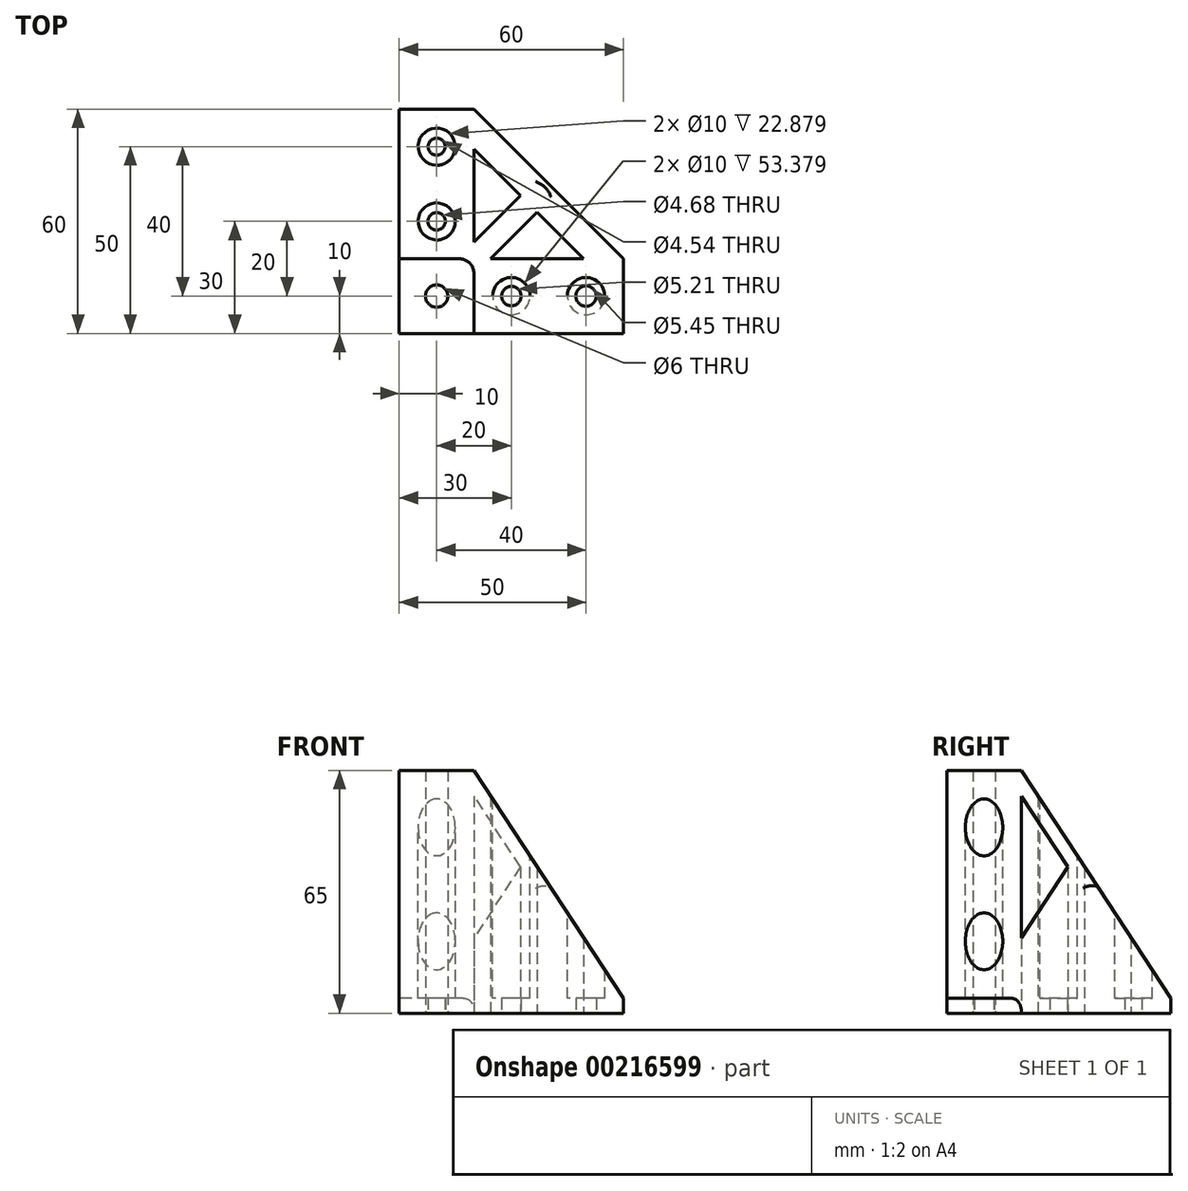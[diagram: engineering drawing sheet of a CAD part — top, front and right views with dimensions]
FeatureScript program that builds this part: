
annotation { "Feature Type Name" : "Feature", "Feature Type Description" : "" }
export const myFeature = defineFeature(function(context is Context, id is Id, definition is map)
    precondition{}
    {
        {
            var Q0;
            Q0=qCreatedBy(makeId("Top.planeOp"),FACE);
            var sketch = newSketch(context, id + "F0", { "sketchPlane" : qUnion([Q0])});
            skLineSegment(sketch, "E0", {"start": v(0, 0) * mm, "end": v(0, 60) * mm});
            skLineSegment(sketch, "E1", {"start": v(0, 60) * mm, "end": v(20, 60) * mm});
            skLineSegment(sketch, "E2", {"start": v(0, 0) * mm, "end": v(60, 0) * mm});
            skLineSegment(sketch, "E3", {"start": v(60, 0) * mm, "end": v(60, 20) * mm});
            skLineSegment(sketch, "E4", {"start": v(20, 60) * mm, "end": v(60, 20) * mm});
            skLineSegment(sketch, "E5", {"start": v(20, 49.4) * mm, "end": v(49.4, 20) * mm, "construction": true});
            skLineSegment(sketch, "E6", {"start": v(49.4, 20) * mm, "end": v(20, 20) * mm, "construction": true});
            skLineSegment(sketch, "E7", {"start": v(20, 20) * mm, "end": v(20, 49.4) * mm, "construction": true});
            skLineSegment(sketch, "E8", {"start": v(24.48, 20) * mm, "end": v(36.94, 32.46) * mm});
            skLineSegment(sketch, "E9", {"start": v(20, 20) * mm, "end": v(34.7, 34.7) * mm, "construction": true});
            skLineSegment(sketch, "E10.MirrorCS", {"start": v(20, 24.48) * mm, "end": v(32.46, 36.94) * mm});
            skLineSegment(sketch, "E11", {"start": v(20, 49.4) * mm, "end": v(20, 24.48) * mm});
            skLineSegment(sketch, "E12", {"start": v(20, 49.4) * mm, "end": v(32.46, 36.94) * mm});
            skLineSegment(sketch, "E13", {"start": v(24.48, 20) * mm, "end": v(49.4, 20) * mm});
            skLineSegment(sketch, "E14", {"start": v(36.94, 32.46) * mm, "end": v(49.4, 20) * mm});
            skSolve(sketch);
        }
        {
            var Q0;
            Q0 = qSketchRegion(id + "F0", true);
            extrude(context, id + "F1", {"entities" : qUnion([Q0]), "depth" : 65 * mm});
        }
        {
            var Q0;
            Q0=makeQuery(id+"F1.opExtrude","SWEPT_FACE",FACE,{"disambiguationData":[OSD([sQuery(id+"F0.wireOp",EDGE,"E2")])]});
            var sketch = newSketch(context, id + "F2", { "sketchPlane" : qUnion([Q0])});
            skLineSegment(sketch, "E15", {"start": v(20, 65) * mm, "end": v(60, 4) * mm});
            skLineSegment(sketch, "E16", {"start": v(60, 4) * mm, "end": v(60, 65) * mm});
            skLineSegment(sketch, "E17", {"start": v(60, 65) * mm, "end": v(20, 65) * mm});
            skSolve(sketch);
        }
        {
            var Q0;
            Q0 = qSketchRegion(id + "F2", true);
            extrude(context, id + "F3", {"entities" : qUnion([Q0]), "operationType" : NewBodyOperationType.REMOVE, "endBound" : BoundingType.THROUGH_ALL, "oppositeDirection" : true, "depth" : 25 * mm});
        }
        {
            var Q0;
            Q0=makeQuery(id+"F1.opExtrude","SWEPT_FACE",FACE,{"disambiguationData":[OSD([sQuery(id+"F0.wireOp",EDGE,"E0")])]});
            var sketch = newSketch(context, id + "F4", { "sketchPlane" : qUnion([Q0])});
            skLineSegment(sketch, "E18", {"start": v(-60, 4) * mm, "end": v(-20, 65) * mm});
            skLineSegment(sketch, "E19", {"start": v(-20, 65) * mm, "end": v(-60, 65) * mm});
            skLineSegment(sketch, "E20", {"start": v(-60, 65) * mm, "end": v(-60, 4) * mm});
            skSolve(sketch);
        }
        {
            var Q0;
            Q0 = qSketchRegion(id + "F4", true);
            extrude(context, id + "F5", {"entities" : qUnion([Q0]), "operationType" : NewBodyOperationType.REMOVE, "endBound" : BoundingType.THROUGH_ALL, "oppositeDirection" : true, "depth" : 25 * mm});
        }
        {
            var Q0;
            Q0=makeQuery(id+"F1.opExtrude","CAP_FACE",FACE,{"disambiguationData":[OSD([sQuery(id+"F0.wireOp",EDGE,"E0"),sQuery(id+"F0.wireOp",EDGE,"E1"),sQuery(id+"F0.wireOp",EDGE,"E2"),sQuery(id+"F0.wireOp",EDGE,"E3"),sQuery(id+"F0.wireOp",EDGE,"E4"),sQuery(id+"F0.wireOp",EDGE,"E8"),sQuery(id+"F0.wireOp",EDGE,"E10.MirrorCS"),sQuery(id+"F0.wireOp",EDGE,"E11"),sQuery(id+"F0.wireOp",EDGE,"E12"),sQuery(id+"F0.wireOp",EDGE,"E13"),sQuery(id+"F0.wireOp",EDGE,"E14")])],"isStart":true});
            var sketch = newSketch(context, id + "F6", { "sketchPlane" : qUnion([Q0])});
            skCircle(sketch, "E21", {"center": v(10, -10) * mm, "radius": 2.5 * mm});
            skCircle(sketch, "E22", {"center": v(30, -10) * mm, "radius": 2.6 * mm});
            skCircle(sketch, "E23", {"center": v(50, -10) * mm, "radius": 2.73 * mm});
            skCircle(sketch, "E24", {"center": v(10, -30) * mm, "radius": 2.34 * mm});
            skCircle(sketch, "E25", {"center": v(10, -50) * mm, "radius": 2.27 * mm});
            skSolve(sketch);
        }
        {
            var Q0;
            Q0 = qSketchRegion(id + "F6", true);
            extrude(context, id + "F7", {"entities" : qUnion([Q0]), "operationType" : NewBodyOperationType.REMOVE, "endBound" : BoundingType.THROUGH_ALL, "oppositeDirection" : true, "depth" : 25 * mm});
        }
        {
            var Q0;
            Q0=makeQuery(id+"F1.opExtrude","CAP_FACE",FACE,{"disambiguationData":[OSD([sQuery(id+"F0.wireOp",EDGE,"E0"),sQuery(id+"F0.wireOp",EDGE,"E1"),sQuery(id+"F0.wireOp",EDGE,"E2"),sQuery(id+"F0.wireOp",EDGE,"E3"),sQuery(id+"F0.wireOp",EDGE,"E4"),sQuery(id+"F0.wireOp",EDGE,"E8"),sQuery(id+"F0.wireOp",EDGE,"E10.MirrorCS"),sQuery(id+"F0.wireOp",EDGE,"E11"),sQuery(id+"F0.wireOp",EDGE,"E12"),sQuery(id+"F0.wireOp",EDGE,"E13"),sQuery(id+"F0.wireOp",EDGE,"E14")])],"isStart":false});
            var sketch = newSketch(context, id + "F8", { "sketchPlane" : qUnion([Q0])});
            skCircle(sketch, "E26.0", {"center": v(10, 50) * mm, "radius": 2.27 * mm, "construction": true});
            skCircle(sketch, "E27.0", {"center": v(10, 30) * mm, "radius": 2.34 * mm, "construction": true});
            skCircle(sketch, "E28.0", {"center": v(10, 10) * mm, "radius": 2.5 * mm, "construction": true});
            skCircle(sketch, "E29.0", {"center": v(30, 10) * mm, "radius": 2.6 * mm, "construction": true});
            skCircle(sketch, "E30.0", {"center": v(50, 10) * mm, "radius": 2.73 * mm, "construction": true});
            skCircle(sketch, "E31", {"center": v(30, 10) * mm, "radius": 5 * mm});
            skCircle(sketch, "E32", {"center": v(50, 10) * mm, "radius": 5 * mm});
            skCircle(sketch, "E33", {"center": v(10, 30) * mm, "radius": 5 * mm});
            skCircle(sketch, "E34", {"center": v(10, 50) * mm, "radius": 5 * mm});
            skSolve(sketch);
        }
        {
            var Q0;
            Q0 = qSketchRegion(id + "F8", true);
            extrude(context, id + "F9", {"entities" : qUnion([Q0]), "operationType" : NewBodyOperationType.REMOVE, "oppositeDirection" : true, "depth" : 61 * mm});
        }
        {
            var Q0;
            Q0=makeQuery(id+"F3.boolean.opBoolean","INTERSECT",EDGE,{"derivedFrom":[makeQuery(id+"F1.opExtrude","SWEPT_FACE",FACE,{"disambiguationData":[OSD([sQuery(id+"F0.wireOp",EDGE,"E4")])]}),makeQuery(id+"F3.opExtrude","SWEPT_FACE",FACE,{"disambiguationData":[OSD([sQuery(id+"F2.wireOp",EDGE,"E15")])]})]});
            var Q1;
            Q1=makeQuery(id+"F5.boolean.opBoolean","INTERSECT",EDGE,{"derivedFrom":[makeQuery(id+"F1.opExtrude","SWEPT_FACE",FACE,{"disambiguationData":[OSD([sQuery(id+"F0.wireOp",EDGE,"E4")])]}),makeQuery(id+"F5.opExtrude","SWEPT_FACE",FACE,{"disambiguationData":[OSD([sQuery(id+"F4.wireOp",EDGE,"E18")])]})]});
            var Q2;
            Q2=makeQuery(id+"F3.boolean.opBoolean","COPY",EDGE,{"derivedFrom":makeQuery(id+"F3.opExtrude","SWEPT_EDGE",EDGE,{"disambiguationData":[OSD([sQuery(id+"F0.wireOp",EDGE,"E2"),sQuery(id+"F0.wireOp",EDGE,"E3"),sQuery(id+"F2.wireOp",EDGE,"E15"),sQuery(id+"F2.wireOp",EDGE,"E16")])]})});
            var Q3;
            Q3=makeQuery(id+"F5.boolean.opBoolean","COPY",EDGE,{"derivedFrom":makeQuery(id+"F5.opExtrude","SWEPT_EDGE",EDGE,{"disambiguationData":[OSD([sQuery(id+"F0.wireOp",EDGE,"E0"),sQuery(id+"F0.wireOp",EDGE,"E1"),sQuery(id+"F4.wireOp",EDGE,"E18"),sQuery(id+"F4.wireOp",EDGE,"E20")])]})});
            var Q4;
            Q4=makeQuery(id+"F5.boolean.opBoolean","INTERSECT",EDGE,{"derivedFrom":[makeQuery(id+"F3.boolean.opBoolean","COPY",FACE,{"derivedFrom":makeQuery(id+"F3.opExtrude","SWEPT_FACE",FACE,{"disambiguationData":[OSD([sQuery(id+"F2.wireOp",EDGE,"E15")])]})}),makeQuery(id+"F5.opExtrude","SWEPT_FACE",FACE,{"disambiguationData":[OSD([sQuery(id+"F4.wireOp",EDGE,"E18")])]})]});
            fillet(context, id + "F10", {"entities" : qUnion([Q0, Q1, Q2, Q3, Q4]), "radius" : 5 * mm, "tangentPropagation" : true, "allowEdgeOverflow" : false});
        }
        {
            var Q0;
            Q0=makeQuery(id+"F1.opExtrude","CAP_FACE",FACE,{"disambiguationData":[OSD([sQuery(id+"F0.wireOp",EDGE,"E0"),sQuery(id+"F0.wireOp",EDGE,"E1"),sQuery(id+"F0.wireOp",EDGE,"E2"),sQuery(id+"F0.wireOp",EDGE,"E3"),sQuery(id+"F0.wireOp",EDGE,"E4"),sQuery(id+"F0.wireOp",EDGE,"E8"),sQuery(id+"F0.wireOp",EDGE,"E10.MirrorCS"),sQuery(id+"F0.wireOp",EDGE,"E11"),sQuery(id+"F0.wireOp",EDGE,"E12"),sQuery(id+"F0.wireOp",EDGE,"E13"),sQuery(id+"F0.wireOp",EDGE,"E14")])],"isStart":true});
            var sketch = newSketch(context, id + "F11", { "sketchPlane" : qUnion([Q0])});
            skCircle(sketch, "E35", {"center": v(10, -10) * mm, "radius": 3 * mm});
            skSolve(sketch);
        }
        {
            var Q0;
            Q0 = qSketchRegion(id + "F11", true);
            extrude(context, id + "F12", {"entities" : qUnion([Q0]), "operationType" : NewBodyOperationType.REMOVE, "endBound" : BoundingType.THROUGH_ALL, "oppositeDirection" : true, "depth" : 25 * mm});
        }
    });
